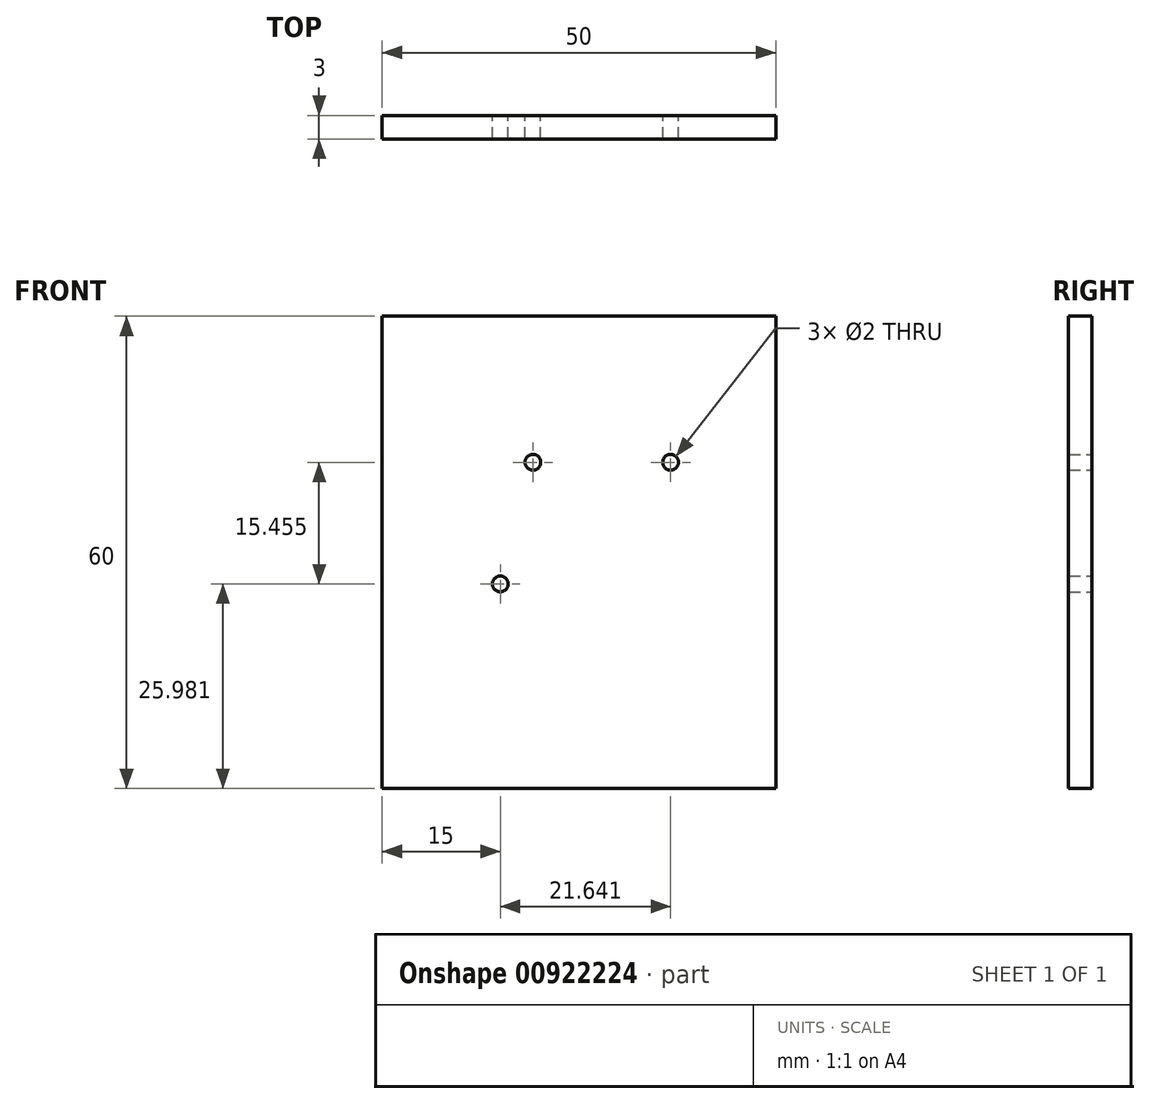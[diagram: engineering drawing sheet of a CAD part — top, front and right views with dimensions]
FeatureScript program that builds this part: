
annotation { "Feature Type Name" : "Feature", "Feature Type Description" : "" }
export const myFeature = defineFeature(function(context is Context, id is Id, definition is map)
    precondition{}
    {
        {
            var Q0;
            Q0=qCreatedBy(makeId("Front.planeOp"),FACE);
            var sketch = newSketch(context, id + "F0", { "sketchPlane" : qUnion([Q0])});
            skLineSegment(sketch, "E0.bottom", {"start": v(0, 0) * mm, "end": v(50, 0) * mm});
            skLineSegment(sketch, "E0.top", {"start": v(0, 60) * mm, "end": v(50, 60) * mm});
            skLineSegment(sketch, "E0.left", {"start": v(0, 0) * mm, "end": v(0, 60) * mm});
            skLineSegment(sketch, "E0.right", {"start": v(50, 0) * mm, "end": v(50, 60) * mm});
            skLineSegment(sketch, "E1", {"start": v(0, 0) * mm, "end": v(15, 25.98) * mm, "construction": true});
            skCircle(sketch, "E2", {"center": v(15, 25.98) * mm, "radius": 1 * mm});
            skLineSegment(sketch, "E3", {"start": v(15, 25.98) * mm, "end": v(18, 25.98) * mm, "construction": true});
            skLineSegment(sketch, "E4", {"start": v(15, 25.98) * mm, "end": v(19.14, 41.44) * mm, "construction": true});
            skCircle(sketch, "E5", {"center": v(19.14, 41.44) * mm, "radius": 1 * mm});
            skLineSegment(sketch, "E6", {"start": v(19.14, 41.44) * mm, "end": v(36.64, 41.44) * mm, "construction": true});
            skCircle(sketch, "E7", {"center": v(36.64, 41.44) * mm, "radius": 1 * mm});
            skSolve(sketch);
        }
        {
            var Q0;
            Q0 = qSketchRegion(id + "F0", true);
            extrude(context, id + "F1", {"entities" : qUnion([Q0]), "depth" : 3 * mm, "offsetDistance" : 25 * mm});
        }
    });
